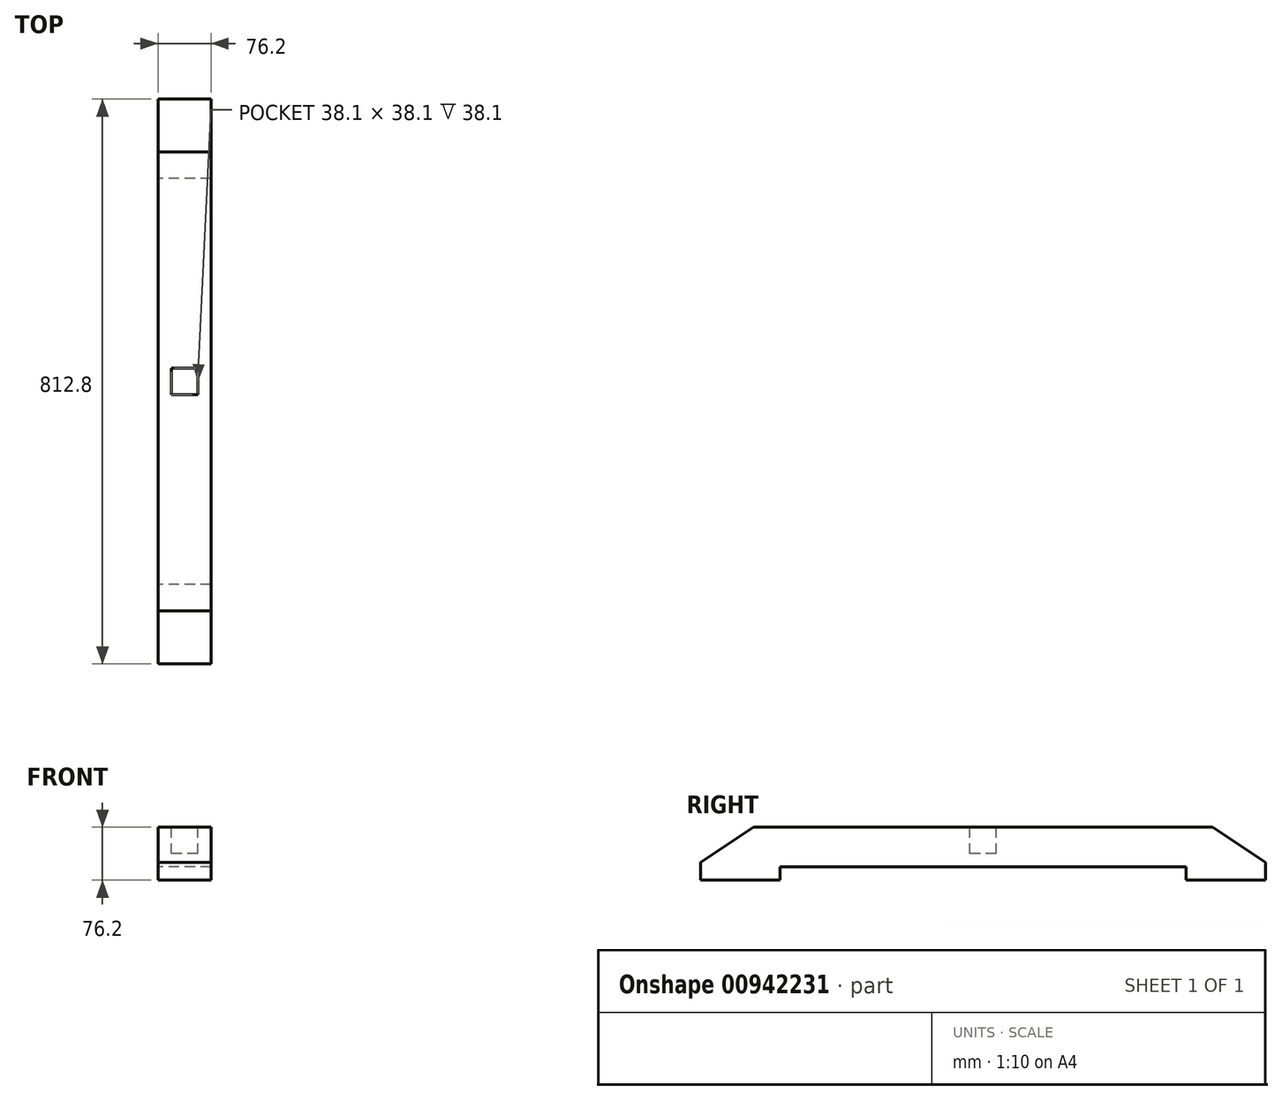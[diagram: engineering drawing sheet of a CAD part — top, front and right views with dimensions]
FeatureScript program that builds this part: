
annotation { "Feature Type Name" : "Feature", "Feature Type Description" : "" }
export const myFeature = defineFeature(function(context is Context, id is Id, definition is map)
    precondition{}
    {
        {
            var Q0;
            Q0=qCreatedBy(makeId("Right.planeOp"),FACE);
            var sketch = newSketch(context, id + "F0", { "sketchPlane" : qUnion([Q0])});
            skLineSegment(sketch, "E0.bottom", {"start": v(330.2, 38.1) * mm, "end": v(-330.2, 38.1) * mm});
            skLineSegment(sketch, "E0.top", {"start": v(406.4, -38.1) * mm, "end": v(292.1, -38.1) * mm});
            skLineSegment(sketch, "E0.left", {"start": v(406.4, -12.7) * mm, "end": v(406.4, -38.1) * mm});
            skLineSegment(sketch, "E0.right", {"start": v(-406.4, -12.7) * mm, "end": v(-406.4, -38.1) * mm});
            skPoint(sketch, "E0.middle", {"position": v(0, 0) * mm});
            skPoint(sketch, "E1.middle", {"position": v(0, -38.1) * mm});
            skLineSegment(sketch, "E2.trimOffspring", {"start": v(-292.1, -38.1) * mm, "end": v(-406.4, -38.1) * mm});
            skPoint(sketch, "E3.orphan", {"position": v(292.1, -57.15) * mm});
            skPoint(sketch, "E4.orphan", {"position": v(-292.1, -57.15) * mm});
            skLineSegment(sketch, "E5", {"start": v(-406.4, -38.1) * mm, "end": v(-406.4, -12.7) * mm});
            skLineSegment(sketch, "E6", {"start": v(-406.4, -12.7) * mm, "end": v(-330.2, 38.1) * mm});
            skLineSegment(sketch, "E7.MirrorCS", {"start": v(406.4, -12.7) * mm, "end": v(330.2, 38.1) * mm});
            skPoint(sketch, "E8.orphan", {"position": v(-406.4, 38.1) * mm});
            skPoint(sketch, "E9.orphan", {"position": v(406.4, 38.1) * mm});
            skPoint(sketch, "E1.right.start.orphan", {"position": v(-292.1, -19.05) * mm});
            skPoint(sketch, "E1.left.start.orphan", {"position": v(292.1, -19.05) * mm});
            skLineSegment(sketch, "E10", {"start": v(-292.1, -38.1) * mm, "end": v(-292.1, -19.05) * mm});
            skLineSegment(sketch, "E11", {"start": v(292.1, -19.05) * mm, "end": v(292.1, -38.1) * mm});
            skLineSegment(sketch, "E12", {"start": v(-292.1, -19.05) * mm, "end": v(292.1, -19.05) * mm});
            skSolve(sketch);
        }
        {
            var Q0;
            Q0 = qSketchRegion(id + "F0", true);
            extrude(context, id + "F1", {"entities" : qUnion([Q0]), "depth" : 76.2 * mm, "offsetDistance" : 25.4 * mm});
        }
        {
            var Q0;
            Q0=makeQuery(id+"F1.opExtrude","SWEPT_FACE",FACE,{"disambiguationData":[OSD([sQuery(id+"F0.wireOp",EDGE,"E0.bottom")])]});
            var sketch = newSketch(context, id + "F2", { "sketchPlane" : qUnion([Q0])});
            skLineSegment(sketch, "E13", {"start": v(0, 0) * mm, "end": v(76.2, 0) * mm});
            skLineSegment(sketch, "E14.bottom", {"start": v(57.15, 19.05) * mm, "end": v(19.05, 19.05) * mm});
            skLineSegment(sketch, "E14.top", {"start": v(57.15, -19.05) * mm, "end": v(19.05, -19.05) * mm});
            skLineSegment(sketch, "E14.left", {"start": v(57.15, 19.05) * mm, "end": v(57.15, -19.05) * mm});
            skLineSegment(sketch, "E14.right", {"start": v(19.05, 19.05) * mm, "end": v(19.05, -19.05) * mm});
            skPoint(sketch, "E14.middle", {"position": v(38.1, 0) * mm});
            skSolve(sketch);
        }
        {
            var Q0;
            Q0 = qSketchRegion(id + "F2", true);
            extrude(context, id + "F3", {"entities" : qUnion([Q0]), "operationType" : NewBodyOperationType.REMOVE, "oppositeDirection" : true, "depth" : 38.1 * mm, "offsetDistance" : 25.4 * mm});
        }
    });
